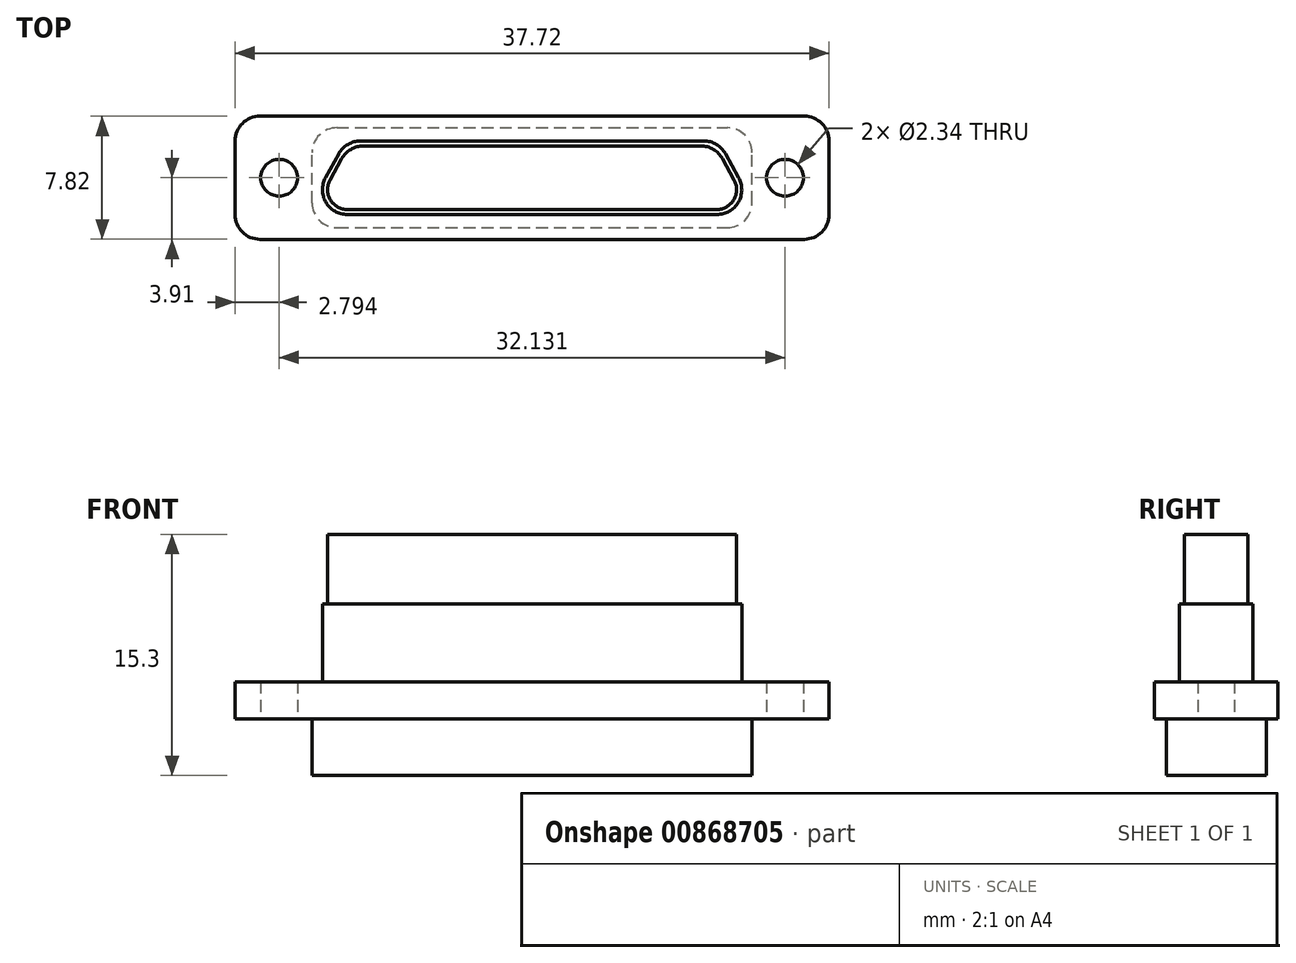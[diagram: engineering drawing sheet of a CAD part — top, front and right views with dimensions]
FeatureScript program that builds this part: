
annotation { "Feature Type Name" : "Feature", "Feature Type Description" : "" }
export const myFeature = defineFeature(function(context is Context, id is Id, definition is map)
    precondition{}
    {
        {
            var Q0;
            Q0=qCreatedBy(makeId("Top.planeOp"),FACE);
            var sketch = newSketch(context, id + "F0", { "sketchPlane" : qUnion([Q0])});
            skLineSegment(sketch, "E0.bottom", {"start": v(-17.28, 3.91) * mm, "end": v(17.28, 3.91) * mm});
            skLineSegment(sketch, "E0.top", {"start": v(-17.28, -3.91) * mm, "end": v(17.28, -3.91) * mm});
            skLineSegment(sketch, "E0.left", {"start": v(-18.86, 2.34) * mm, "end": v(-18.86, -2.34) * mm});
            skLineSegment(sketch, "E0.right", {"start": v(18.86, 2.34) * mm, "end": v(18.86, -2.34) * mm});
            skPoint(sketch, "E0.middle", {"position": v(0, 0) * mm});
            skCircle(sketch, "E1", {"center": v(-16.07, 0) * mm, "radius": 1.17 * mm});
            skCircle(sketch, "E2", {"center": v(16.07, 0) * mm, "radius": 1.17 * mm});
            skPoint(sketch, "E3.visualSharp", {"position": v(-18.86, -3.91) * mm});
            skArc(sketch, "E3.filletArc", {"start": v(-18.86, -2.34) * mm, "mid": v(-18.4, -3.45) * mm, "end": v(-17.28, -3.91) * mm});
            skPoint(sketch, "E4.visualSharp", {"position": v(-18.86, 3.91) * mm});
            skArc(sketch, "E4.filletArc", {"start": v(-17.28, 3.91) * mm, "mid": v(-18.4, 3.45) * mm, "end": v(-18.86, 2.34) * mm});
            skPoint(sketch, "E5.visualSharp", {"position": v(18.86, 3.91) * mm});
            skArc(sketch, "E5.filletArc", {"start": v(18.86, 2.34) * mm, "mid": v(18.4, 3.45) * mm, "end": v(17.28, 3.91) * mm});
            skPoint(sketch, "E6.visualSharp", {"position": v(18.86, -3.91) * mm});
            skArc(sketch, "E6.filletArc", {"start": v(17.28, -3.91) * mm, "mid": v(18.4, -3.45) * mm, "end": v(18.86, -2.34) * mm});
            skSolve(sketch);
        }
        {
            var Q0;
            Q0=makeQuery(id+"F0.imprint","IMPRINT",FACE,{"disambiguationData":[TD([[makeQuery(id+"F0.imprint","IMPRINT",EDGE,{"derivedFrom":sQuery(id+"F0.wireOp",EDGE,"E0.bottom")}),-1.0]])]});
            extrude(context, id + "F1", {"entities" : qUnion([Q0]), "endBound" : BoundingType.SYMMETRIC, "depth" : 2.36 * mm, "offsetDistance" : 25.4 * mm});
        }
        {
            var Q0;
            Q0=makeQuery(id+"F1.opExtrude","CAP_FACE",FACE,{"disambiguationData":[OSD([sQuery(id+"F0.wireOp",EDGE,"E0.bottom"),sQuery(id+"F0.wireOp",EDGE,"E0.top"),sQuery(id+"F0.wireOp",EDGE,"E0.left"),sQuery(id+"F0.wireOp",EDGE,"E0.right"),sQuery(id+"F0.wireOp",EDGE,"E1"),sQuery(id+"F0.wireOp",EDGE,"E2"),sQuery(id+"F0.wireOp",EDGE,"E3.filletArc"),sQuery(id+"F0.wireOp",EDGE,"E4.filletArc"),sQuery(id+"F0.wireOp",EDGE,"E5.filletArc"),sQuery(id+"F0.wireOp",EDGE,"E6.filletArc")])],"isStart":false});
            var sketch = newSketch(context, id + "F2", { "sketchPlane" : qUnion([Q0])});
            skPoint(sketch, "E7.middle", {"position": v(0, 0) * mm});
            skLineSegment(sketch, "E8.top", {"start": v(11.74, -2.34) * mm, "end": v(-11.74, -2.34) * mm});
            skLineSegment(sketch, "E9", {"start": v(-10.9, 2.34) * mm, "end": v(10.9, 2.34) * mm});
            skLineSegment(sketch, "E10", {"start": v(-13.12, 0) * mm, "end": v(-12.27, 1.53) * mm});
            skLineSegment(sketch, "E11", {"start": v(12.28, 1.53) * mm, "end": v(13.12, 0) * mm});
            skPoint(sketch, "E12.visualSharp", {"position": v(-11.82, 2.34) * mm});
            skArc(sketch, "E12.filletArc", {"start": v(-10.9, 2.34) * mm, "mid": v(-11.7, 2.12) * mm, "end": v(-12.27, 1.53) * mm});
            skPoint(sketch, "E13.visualSharp", {"position": v(-14.41, -2.34) * mm});
            skArc(sketch, "E13.filletArc", {"start": v(-13.12, 0) * mm, "mid": v(-13.1, -1.56) * mm, "end": v(-11.74, -2.34) * mm});
            skPoint(sketch, "E14.visualSharp", {"position": v(14.42, -2.34) * mm});
            skArc(sketch, "E14.filletArc", {"start": v(11.74, -2.34) * mm, "mid": v(13.1, -1.56) * mm, "end": v(13.12, 0) * mm});
            skPoint(sketch, "E15.visualSharp", {"position": v(11.83, 2.34) * mm});
            skArc(sketch, "E15.filletArc", {"start": v(12.28, 1.53) * mm, "mid": v(11.7, 2.12) * mm, "end": v(10.9, 2.34) * mm});
            skSolve(sketch);
        }
        {
            var Q0;
            Q0=qSketchRegion(id+"F2",true);
            extrude(context, id + "F3", {"entities" : qUnion([Q0]), "operationType" : NewBodyOperationType.ADD, "depth" : 4.95 * mm, "offsetDistance" : 25.4 * mm});
        }
        {
            var Q0;
            Q0=makeQuery(id+"F1.opExtrude","CAP_FACE",FACE,{"disambiguationData":[OSD([sQuery(id+"F0.wireOp",EDGE,"E0.bottom"),sQuery(id+"F0.wireOp",EDGE,"E0.top"),sQuery(id+"F0.wireOp",EDGE,"E0.left"),sQuery(id+"F0.wireOp",EDGE,"E0.right"),sQuery(id+"F0.wireOp",EDGE,"E1"),sQuery(id+"F0.wireOp",EDGE,"E2"),sQuery(id+"F0.wireOp",EDGE,"E3.filletArc"),sQuery(id+"F0.wireOp",EDGE,"E4.filletArc"),sQuery(id+"F0.wireOp",EDGE,"E5.filletArc"),sQuery(id+"F0.wireOp",EDGE,"E6.filletArc")])],"isStart":true});
            var sketch = newSketch(context, id + "F4", { "sketchPlane" : qUnion([Q0])});
            skLineSegment(sketch, "E16.bottom", {"start": v(-12.4, 3.18) * mm, "end": v(12.4, 3.18) * mm});
            skLineSegment(sketch, "E16.top", {"start": v(-12.4, -3.18) * mm, "end": v(12.4, -3.18) * mm});
            skLineSegment(sketch, "E16.left", {"start": v(-13.97, 1.6) * mm, "end": v(-13.97, -1.6) * mm});
            skLineSegment(sketch, "E16.right", {"start": v(13.97, 1.6) * mm, "end": v(13.97, -1.6) * mm});
            skPoint(sketch, "E16.middle", {"position": v(0, 0) * mm});
            skPoint(sketch, "E17.visualSharp", {"position": v(-13.97, 3.17) * mm});
            skArc(sketch, "E17.filletArc", {"start": v(-12.4, 3.18) * mm, "mid": v(-13.5, 2.71) * mm, "end": v(-13.97, 1.6) * mm});
            skPoint(sketch, "E18.visualSharp", {"position": v(-13.97, -3.18) * mm});
            skArc(sketch, "E18.filletArc", {"start": v(-13.97, -1.6) * mm, "mid": v(-13.5, -2.71) * mm, "end": v(-12.4, -3.17) * mm});
            skPoint(sketch, "E19.visualSharp", {"position": v(13.97, -3.18) * mm});
            skArc(sketch, "E19.filletArc", {"start": v(12.4, -3.18) * mm, "mid": v(13.5, -2.71) * mm, "end": v(13.97, -1.6) * mm});
            skPoint(sketch, "E20.visualSharp", {"position": v(13.97, 3.18) * mm});
            skArc(sketch, "E20.filletArc", {"start": v(13.97, 1.6) * mm, "mid": v(13.5, 2.71) * mm, "end": v(12.4, 3.18) * mm});
            skSolve(sketch);
        }
        {
            var Q0;
            Q0=qSketchRegion(id+"F4",true);
            extrude(context, id + "F5", {"entities" : qUnion([Q0]), "operationType" : NewBodyOperationType.ADD, "depth" : 3.58 * mm, "offsetDistance" : 25.4 * mm});
        }
        {
            var Q0;
            Q0=makeQuery(id+"F3.opExtrude","CAP_FACE",FACE,{"disambiguationData":[OSD([sQuery(id+"F2.wireOp",EDGE,"E8.top"),sQuery(id+"F2.wireOp",EDGE,"E9"),sQuery(id+"F2.wireOp",EDGE,"E10"),sQuery(id+"F2.wireOp",EDGE,"E11"),sQuery(id+"F2.wireOp",EDGE,"E12.filletArc"),sQuery(id+"F2.wireOp",EDGE,"E13.filletArc"),sQuery(id+"F2.wireOp",EDGE,"E14.filletArc"),sQuery(id+"F2.wireOp",EDGE,"E15.filletArc")])],"isStart":false});
            var sketch = newSketch(context, id + "F6", { "sketchPlane" : qUnion([Q0])});
            skLineSegment(sketch, "E21", {"start": v(-10.7, 2.02) * mm, "end": v(10.71, 2.02) * mm});
            skLineSegment(sketch, "E22", {"start": v(12.09, 1.2) * mm, "end": v(12.83, -0.13) * mm});
            skLineSegment(sketch, "E23", {"start": v(11.72, -2.02) * mm, "end": v(-11.72, -2.02) * mm});
            skLineSegment(sketch, "E24", {"start": v(-12.83, -0.13) * mm, "end": v(-12.09, 1.2) * mm});
            skPoint(sketch, "E25.visualSharp", {"position": v(-13.88, -2.02) * mm});
            skArc(sketch, "E25.filletArc", {"start": v(-12.83, -0.13) * mm, "mid": v(-12.81, -1.4) * mm, "end": v(-11.72, -2.02) * mm});
            skPoint(sketch, "E26.visualSharp", {"position": v(-11.64, 2.02) * mm});
            skArc(sketch, "E26.filletArc", {"start": v(-10.7, 2.02) * mm, "mid": v(-11.5, 1.8) * mm, "end": v(-12.09, 1.2) * mm});
            skPoint(sketch, "E27.visualSharp", {"position": v(11.64, 2.02) * mm});
            skArc(sketch, "E27.filletArc", {"start": v(12.09, 1.2) * mm, "mid": v(11.5, 1.8) * mm, "end": v(10.71, 2.02) * mm});
            skPoint(sketch, "E28.visualSharp", {"position": v(13.88, -2.02) * mm});
            skArc(sketch, "E28.filletArc", {"start": v(11.72, -2.02) * mm, "mid": v(12.82, -1.4) * mm, "end": v(12.83, -0.13) * mm});
            skSolve(sketch);
        }
        {
            var Q0;
            Q0=qSketchRegion(id+"F6",true);
            extrude(context, id + "F7", {"entities" : qUnion([Q0]), "operationType" : NewBodyOperationType.ADD, "depth" : 4.4 * mm, "offsetDistance" : 25.4 * mm});
        }
    });
